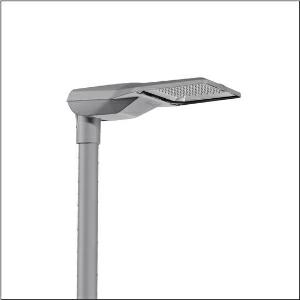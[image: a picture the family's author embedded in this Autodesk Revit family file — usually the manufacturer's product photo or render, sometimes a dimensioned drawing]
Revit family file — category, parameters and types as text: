
# Revit family: streetlight_sl_21_iq_midi___st1_0a_5xe3d41g08mb_322d
name_source: partatom
category: Lighting Fixtures
units: mm (PartAtom-declared; Revit-internal decimal feet)

## family parameters
Cut with Voids When Loaded = No
Host = Face
Light Source = No
Part Type = Normal
Room Calculation Point = No
Round Connector Dimension = Use Diameter
Shared = No

## types (1)
- --- (1 x LED, 20360 lm, 146.7 W, 4000K)
    Apparent Load = 147 VA
    CIE Flux Codes = 37 72 97 100 100
    Color Rendering = 70
    Color Temperature = 4000K
    Default Elevation = 1800 mm
    Description = Streetlight SL 21 iQ midi, mast luminaire, primary light control with lens, of PMMA, primary optical cover: cover, of toughened safety glass, transparent, light distribution: ST1.0a, light emission: direct distribution, primary light characteristic: asymmetric, installation type: post-top, side-entry, LED, High Power LED, rated luminous flux: 20.360lm, luminous efficacy: 139lm/W, light colour: 740, colour temperature: 4000K, control: Street-Remote, Auto-Match, Temp-Guard, Lumen-Switch, Night-Set, Smart-Wire, Light-Fading, Desk-Remote (wireless, voltage-free reading and setting of iQ features in the workshop via application-optimized NFC function/RFID function), optimised constant luminous flux control (CLO 2.0), pre-setting: linear dimming characteristic, mains connection: 230..240V, AC, 50/60Hz, start of lifetime: 147W, end of service life: 161W, reduction: 62W, luminaire housing, of diecast aluminium, powder-coated, Siteco® metallic grey (DB 702S), corrosivity category C5 mid according to DIN EN ISO 12944, please order mast flange separately, inclination adjustable: 0°, 5°, 10°, 15°, sealing non-destructively replaceable, multi-level sealing system, length: 644mm, width: 335mm, height: 110mm, mast flange for spigot size: 42mm (side-entry): 5XC10008XM4, 60/48mm (side-entry/post-top): 5XC10108XM2, 76/60mm (side-entry/post-top): 5XC10108XM1, protection rating (complete): IP66, insulation class (complete): insulation class II (safety insulation), certification: CE, ENEC, ENEC+, VDE, impact resistance: IK09, permissible operating ambient temperature for outdoor applications: -40..+50°C, standard-compliant lighting for roads and squares, packaging unit: 1 piece

Light Distribution: ST1.0a
    Height = 111 mm
    Lamp = 1 x LED
    Lamp Light Flux = 20360 lm
    Lamp Power = 146.7 W
    Lamp count = 1
    Length = 644 mm
    Luminous efficacy = 139 lm/W
    Manufacturer = Siteco
    ModVariant = No
    Model = 5XE3D41G08MB
    Number of Poles = 1
    OnlyDefault = Yes
    Power Factor = 1
    Product Name = Streetlight SL 21 iQ midi | ST1.0a
    Product group = mast luminaire | pylon top
    ProductGroupID = 6100
    Protection Class = Protection class II
    Protection Degree = IP 66
    RLX_Detail_Level = 1
    RLX_Emergency_Light_Flux = 0 lm
    RLX_Emergency_Type = 0
    RLX_Emergency_Type_DB = No
    RlxData = <blob elided: 90689 chars, md5=55981dae>
    Socket = socket
    Standby Power = 0 W
    System Light Flux = 20360 lm
    System Power = 147 W
    Type Comments = factory setting: luminous flux: 100 % | dim-lin: 254 | 753 mA
    Type Image = l_1004298.jpg
    URL = http://relux.com
    VarID = @adj_161799
    Voltage = 0 V
    Weight = 0.00 kg
    Width = 336 mm

## geometry (parser evidence)
native form markers: Blend x4, Sweep x10
no freeform markers — native parametric forms only
